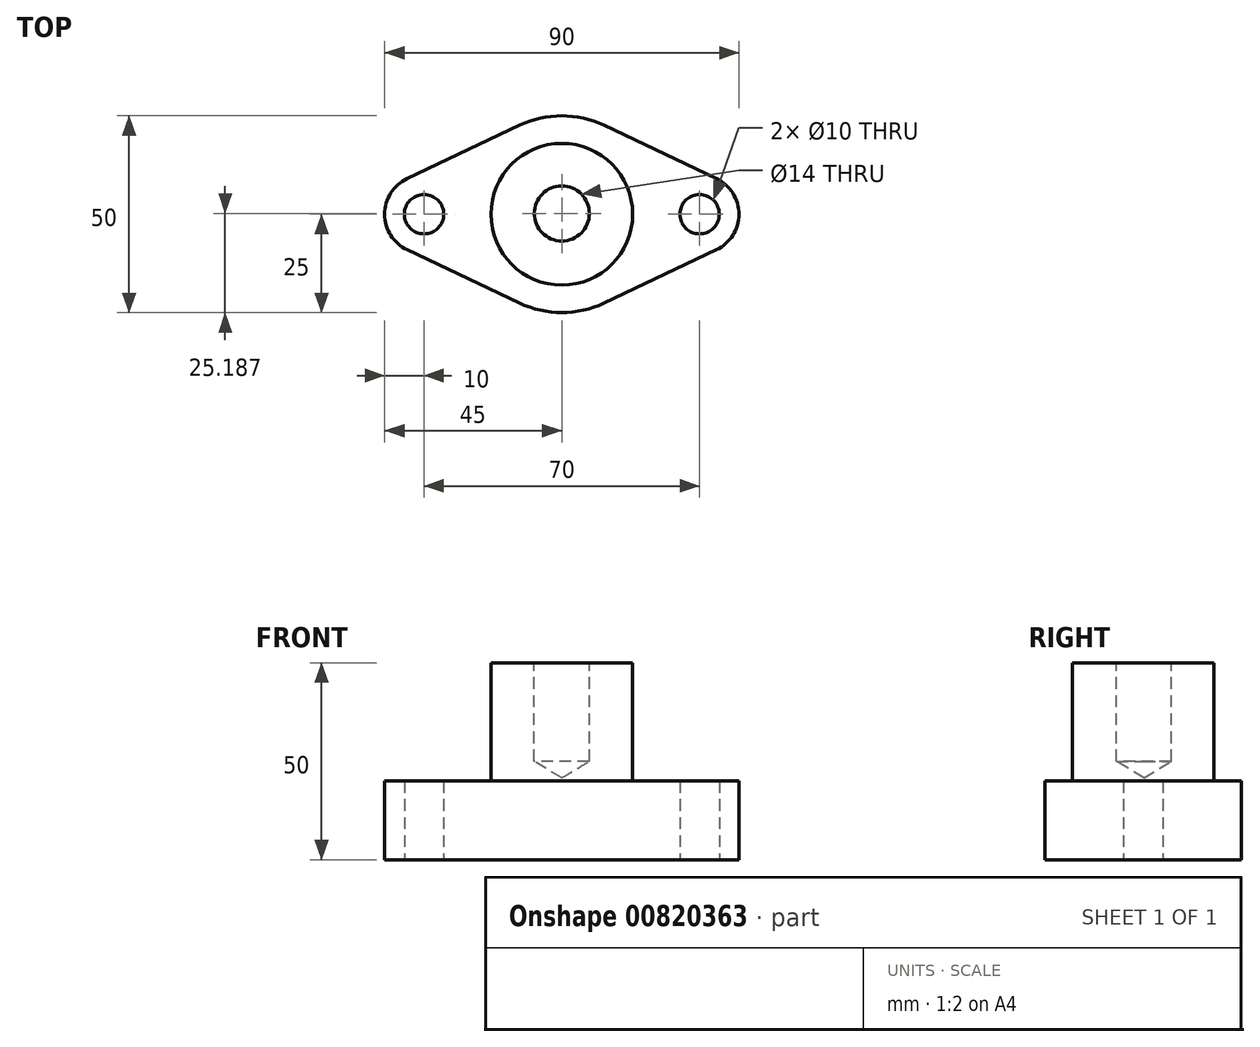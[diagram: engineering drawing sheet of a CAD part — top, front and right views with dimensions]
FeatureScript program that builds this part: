
annotation { "Feature Type Name" : "Feature", "Feature Type Description" : "" }
export const myFeature = defineFeature(function(context is Context, id is Id, definition is map)
    precondition{}
    {
        {
            var Q0;
            Q0=qCreatedBy(makeId("Top.planeOp"),FACE);
            var sketch = newSketch(context, id + "F0", { "sketchPlane" : qUnion([Q0])});
            skCircle(sketch, "E0", {"center": v(0, 0) * mm, "radius": 25 * mm});
            skLineSegment(sketch, "E1", {"start": v(0, 0) * mm, "end": v(-25, 0) * mm});
            skLineSegment(sketch, "E2", {"start": v(-25, 0) * mm, "end": v(-35, 0) * mm});
            skLineSegment(sketch, "E3", {"start": v(0, 0) * mm, "end": v(25, 0) * mm});
            skLineSegment(sketch, "E4", {"start": v(25, 0) * mm, "end": v(35, 0) * mm});
            skCircle(sketch, "E5", {"center": v(-35, 0) * mm, "radius": 10 * mm});
            skCircle(sketch, "E6", {"center": v(35, 0) * mm, "radius": 10 * mm});
            skLineSegment(sketch, "E7", {"start": v(-39.29, 9.04) * mm, "end": v(-10.71, 22.59) * mm});
            skLineSegment(sketch, "E8", {"start": v(-39.29, -9.04) * mm, "end": v(-10.71, -22.59) * mm});
            skLineSegment(sketch, "E9", {"start": v(10.71, 22.59) * mm, "end": v(39.29, 9.04) * mm});
            skLineSegment(sketch, "E10", {"start": v(10.71, -22.59) * mm, "end": v(39.29, -9.04) * mm});
            skCircle(sketch, "E11", {"center": v(0, 0) * mm, "radius": 18 * mm});
            skSolve(sketch);
        }
        {
            var Q0;
            {var subQ3=sQuery(id+"F0.wireOp",EDGE,"E7");Q0=makeQuery(id+"F0.imprint","IMPRINT",FACE,{"disambiguationData":[TD([[makeQuery(id+"F0.imprint","IMPRINT",EDGE,{"derivedFrom":subQ3}),-1.0]])]});}
            var Q1;
            {var subQ0=sQuery(id+"F0.wireOp",EDGE,"E1");Q1=makeQuery(id+"F0.imprint","IMPRINT",FACE,{"disambiguationData":[TD([[makeQuery(id+"F0.imprint","IMPRINT",EDGE,{"derivedFrom":subQ0}),-1.0]])]});}
            var Q2;
            {var subQ0=sQuery(id+"F0.wireOp",EDGE,"E5");var subQ2=makeQuery(id+"F0.imprint","INTERSECT",VERTEX,{"derivedFrom":[subQ0,sQuery(id+"F0.wireOp",EDGE,"E7")]});Q2=makeQuery(id+"F0.imprint","IMPRINT",FACE,{"disambiguationData":[TD([[makeQuery(id+"F0.imprint","IMPRINT",EDGE,{"disambiguationData":[TD([[subQ2,-1.0]])],"derivedFrom":subQ0}),1.0]])]});}
            var Q3;
            {var subQ3=sQuery(id+"F0.wireOp",EDGE,"E8");Q3=makeQuery(id+"F0.imprint","IMPRINT",FACE,{"disambiguationData":[TD([[makeQuery(id+"F0.imprint","IMPRINT",EDGE,{"derivedFrom":subQ3}),1.0]])]});}
            var Q4;
            {var subQ3=sQuery(id+"F0.wireOp",EDGE,"E10");Q4=makeQuery(id+"F0.imprint","IMPRINT",FACE,{"disambiguationData":[TD([[makeQuery(id+"F0.imprint","IMPRINT",EDGE,{"derivedFrom":subQ3}),1.0]])]});}
            var Q5;
            {var subQ0=sQuery(id+"F0.wireOp",EDGE,"E1");Q5=makeQuery(id+"F0.imprint","IMPRINT",FACE,{"disambiguationData":[TD([[makeQuery(id+"F0.imprint","IMPRINT",EDGE,{"derivedFrom":subQ0}),1.0]])]});}
            var Q6;
            {var subQ0=sQuery(id+"F0.wireOp",EDGE,"E6");var subQ2=makeQuery(id+"F0.imprint","INTERSECT",VERTEX,{"derivedFrom":[subQ0,sQuery(id+"F0.wireOp",EDGE,"E9")]});Q6=makeQuery(id+"F0.imprint","IMPRINT",FACE,{"disambiguationData":[TD([[makeQuery(id+"F0.imprint","IMPRINT",EDGE,{"disambiguationData":[TD([[subQ2,1.0]])],"derivedFrom":subQ0}),1.0]])]});}
            var Q7;
            {var subQ3=sQuery(id+"F0.wireOp",EDGE,"E9");Q7=makeQuery(id+"F0.imprint","IMPRINT",FACE,{"disambiguationData":[TD([[makeQuery(id+"F0.imprint","IMPRINT",EDGE,{"derivedFrom":subQ3}),-1.0]])]});}
            var Q8;
            {var subQ1=sQuery(id+"F0.wireOp",EDGE,"E0");var subQ5=makeQuery(id+"F0.imprint","INTERSECT",VERTEX,{"derivedFrom":[subQ1,sQuery(id+"F0.wireOp",EDGE,"E7")]});Q8=makeQuery(id+"F0.imprint","IMPRINT",FACE,{"disambiguationData":[TD([[makeQuery(id+"F0.imprint","IMPRINT",EDGE,{"disambiguationData":[TD([[subQ5,1.0]])],"derivedFrom":subQ1}),1.0]])]});}
            var Q9;
            {var subQ1=sQuery(id+"F0.wireOp",EDGE,"E0");var subQ8=makeQuery(id+"F0.imprint","INTERSECT",VERTEX,{"derivedFrom":[subQ1,sQuery(id+"F0.wireOp",EDGE,"E8")]});Q9=makeQuery(id+"F0.imprint","IMPRINT",FACE,{"disambiguationData":[TD([[makeQuery(id+"F0.imprint","IMPRINT",EDGE,{"disambiguationData":[TD([[subQ8,-1.0]])],"derivedFrom":subQ1}),1.0]])]});}
            extrude(context, id + "F1", {"entities" : qUnion([Q0, Q1, Q2, Q3, Q4, Q5, Q6, Q7, Q8, Q9]), "depth" : 20 * mm, "offsetDistance" : 25 * mm});
        }
        {
            var Q0;
            Q0=makeQuery(id+"F1.opExtrude","CAP_FACE",FACE,{"disambiguationData":[OSD([sQuery(id+"F0.wireOp",EDGE,"E0"),sQuery(id+"F0.wireOp",EDGE,"E5"),sQuery(id+"F0.wireOp",EDGE,"E6"),sQuery(id+"F0.wireOp",EDGE,"E7"),sQuery(id+"F0.wireOp",EDGE,"E8"),sQuery(id+"F0.wireOp",EDGE,"E9"),sQuery(id+"F0.wireOp",EDGE,"E10")])],"isStart":false});
            var sketch = newSketch(context, id + "F2", { "sketchPlane" : qUnion([Q0])});
            skPoint(sketch, "E12", {"position": v(-35, 0) * mm});
            skPoint(sketch, "E13", {"position": v(35, 0) * mm});
            skPoint(sketch, "E14", {"position": v(0, 0) * mm});
            skLineSegment(sketch, "E15", {"start": v(35, 0) * mm, "end": v(-35, 0) * mm});
            skLineSegment(sketch, "E16", {"start": v(0, 0) * mm, "end": v(0, 52.61) * mm});
            skLineSegment(sketch, "E17", {"start": v(0, 0) * mm, "end": v(0, -59.9) * mm});
            skCircle(sketch, "E18", {"center": v(0, 0) * mm, "radius": 18 * mm});
            skSolve(sketch);
        }
        {
            var Q0;
            Q0=sQuery(id+"F0.wireOp",VERTEX,"E5.center");
            var Q1;
            Q1=sQuery(id+"F0.wireOp",VERTEX,"E6.center");
            var Q2;
            Q2=makeQuery(id+"F1.opExtrude","SWEPT_BODY",BODY,{"disambiguationData":[OSD([sQuery(id+"F0.wireOp",EDGE,"E0"),sQuery(id+"F0.wireOp",EDGE,"E5"),sQuery(id+"F0.wireOp",EDGE,"E6"),sQuery(id+"F0.wireOp",EDGE,"E7"),sQuery(id+"F0.wireOp",EDGE,"E8"),sQuery(id+"F0.wireOp",EDGE,"E9"),sQuery(id+"F0.wireOp",EDGE,"E10")])]});
            hole(context, id + "F3", {"style" : HoleStyle.SIMPLE, "endStyle" : HoleEndStyle.THROUGH, "oppositeDirection" : true, "holeDiameter" : 10 * mm, "majorDiameter" : 5 * mm, "isTappedThrough" : true, "tappedDepth" : 12 * mm, "tapClearance" : 3, "locations" : qUnion([Q0, Q1]), "scope" : qUnion([Q2])});
        }
        {
            var Q0;
            {var subQ1=sQuery(id+"F2.wireOp",EDGE,"E15");var subQ3=sQuery(id+"F2.wireOp",EDGE,"E18");var subQ4=makeQuery(id+"F2.imprint","INTERSECT",VERTEX,{"disambiguationData":[OD(1.0)],"derivedFrom":[subQ1,subQ3]});Q0=makeQuery(id+"F2.imprint","IMPRINT",FACE,{"disambiguationData":[TD([[makeQuery(id+"F2.imprint","IMPRINT",EDGE,{"disambiguationData":[TD([[subQ4,-1.0]])],"derivedFrom":subQ3}),1.0]])]});}
            var Q1;
            {var subQ1=sQuery(id+"F2.wireOp",EDGE,"E15");var subQ3=sQuery(id+"F2.wireOp",EDGE,"E18");var subQ4=makeQuery(id+"F2.imprint","INTERSECT",VERTEX,{"disambiguationData":[OD(1.0)],"derivedFrom":[subQ1,subQ3]});Q1=makeQuery(id+"F2.imprint","IMPRINT",FACE,{"disambiguationData":[TD([[makeQuery(id+"F2.imprint","IMPRINT",EDGE,{"disambiguationData":[TD([[subQ4,1.0]])],"derivedFrom":subQ3}),1.0]])]});}
            var Q2;
            {var subQ1=sQuery(id+"F2.wireOp",EDGE,"E15");var subQ3=sQuery(id+"F2.wireOp",EDGE,"E18");var subQ4=makeQuery(id+"F2.imprint","INTERSECT",VERTEX,{"disambiguationData":[OD(0.0)],"derivedFrom":[subQ1,subQ3]});Q2=makeQuery(id+"F2.imprint","IMPRINT",FACE,{"disambiguationData":[TD([[makeQuery(id+"F2.imprint","IMPRINT",EDGE,{"disambiguationData":[TD([[subQ4,-1.0]])],"derivedFrom":subQ3}),1.0]])]});}
            var Q3;
            {var subQ1=sQuery(id+"F2.wireOp",EDGE,"E15");var subQ3=sQuery(id+"F2.wireOp",EDGE,"E18");var subQ4=makeQuery(id+"F2.imprint","INTERSECT",VERTEX,{"disambiguationData":[OD(0.0)],"derivedFrom":[subQ1,subQ3]});Q3=makeQuery(id+"F2.imprint","IMPRINT",FACE,{"disambiguationData":[TD([[makeQuery(id+"F2.imprint","IMPRINT",EDGE,{"disambiguationData":[TD([[subQ4,1.0]])],"derivedFrom":subQ3}),1.0]])]});}
            extrude(context, id + "F4", {"entities" : qUnion([Q0, Q1, Q2, Q3]), "operationType" : NewBodyOperationType.ADD, "depth" : 30 * mm, "offsetDistance" : 25 * mm});
        }
        {
            var Q0;
            Q0=makeQuery(id+"F4.opExtrude","CAP_FACE",FACE,{"disambiguationData":[OSD([sQuery(id+"F2.wireOp",EDGE,"E18")])],"isStart":false});
            var sketch = newSketch(context, id + "F5", { "sketchPlane" : qUnion([Q0])});
            skLineSegment(sketch, "E19", {"start": v(-18, 0.19) * mm, "end": v(18, 0.19) * mm});
            skPoint(sketch, "E20", {"position": v(0, 0.19) * mm});
            skSolve(sketch);
        }
        {
            var Q0;
            Q0=sQuery(id+"F5.wireOp",VERTEX,"E20");
            var Q1;
            Q1=makeQuery(id+"F1.opExtrude","SWEPT_BODY",BODY,{"disambiguationData":[OSD([sQuery(id+"F0.wireOp",EDGE,"E0"),sQuery(id+"F0.wireOp",EDGE,"E5"),sQuery(id+"F0.wireOp",EDGE,"E6"),sQuery(id+"F0.wireOp",EDGE,"E7"),sQuery(id+"F0.wireOp",EDGE,"E8"),sQuery(id+"F0.wireOp",EDGE,"E9"),sQuery(id+"F0.wireOp",EDGE,"E10")])]});
            hole(context, id + "F6", {"style" : HoleStyle.SIMPLE, "endStyle" : HoleEndStyle.BLIND, "standardTappedOrClearance" : lookupTablePath({ "standard" : "ISO", "engagement" : "75%", "pitch" : "2 mm", "size" : "M16", "type" : "Tapped" }), "standardBlindInLast" : lookupTablePath({ "standard" : "ISO", "engagement" : "75%", "pitch" : "2 mm", "size" : "M16", "type" : "Tapped" }), "holeDiameter" : 14 * mm, "majorDiameter" : 16 * mm, "showTappedDepth" : true, "holeDepth" : 25 * mm, "isTappedThrough" : true, "tappedDepth" : 19 * mm, "tapClearance" : 3, "locations" : qUnion([Q0]), "scope" : qUnion([Q1])});
        }
    });
